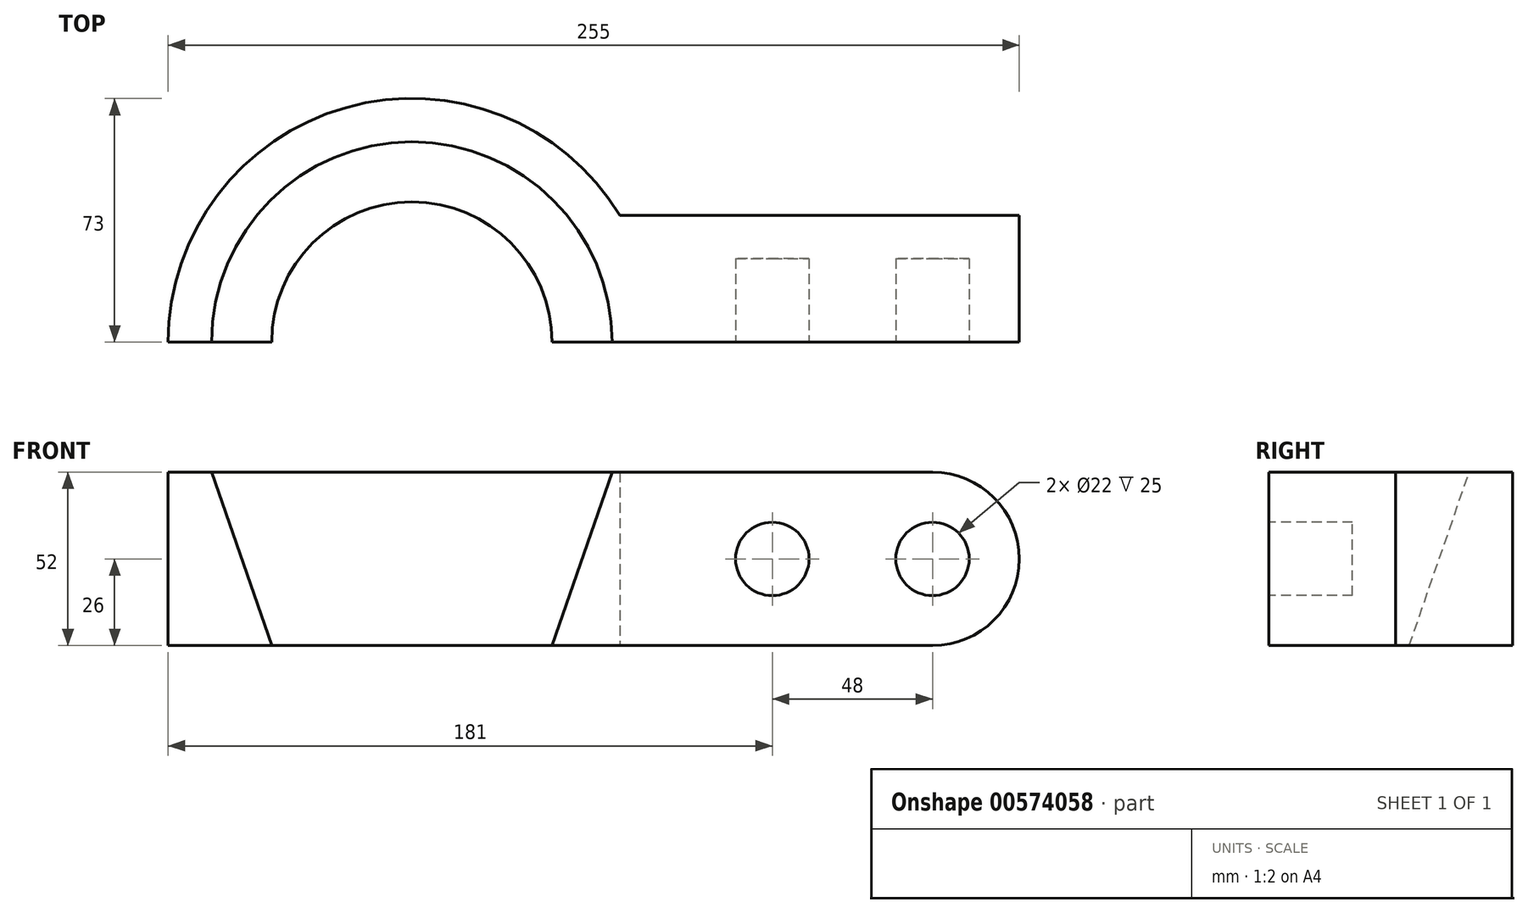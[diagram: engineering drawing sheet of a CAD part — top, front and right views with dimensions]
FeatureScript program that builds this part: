
annotation { "Feature Type Name" : "Feature", "Feature Type Description" : "" }
export const myFeature = defineFeature(function(context is Context, id is Id, definition is map)
    precondition{}
    {
        {
            var Q0;
            Q0=qCreatedBy(makeId("Top.planeOp"),FACE);
            var sketch = newSketch(context, id + "F0", { "sketchPlane" : qUnion([Q0])});
            skArc(sketch, "E0", {"start": v(62.33, 38) * mm, "mid": v(-19.73, 70.28) * mm, "end": v(-73, 0) * mm});
            skLineSegment(sketch, "E1", {"start": v(-73, 0) * mm, "end": v(73, 0) * mm});
            skLineSegment(sketch, "E2", {"start": v(73, 0) * mm, "end": v(182, 0) * mm});
            skLineSegment(sketch, "E3", {"start": v(182, 0) * mm, "end": v(182, 38) * mm});
            skLineSegment(sketch, "E4", {"start": v(182, 38) * mm, "end": v(62.33, 38) * mm});
            skSolve(sketch);
        }
        {
            var Q0;
            Q0=makeQuery(id+"F0.imprint","IMPRINT",FACE,{"disambiguationData":[TD([[makeQuery(id+"F0.imprint","IMPRINT",EDGE,{"derivedFrom":sQuery(id+"F0.wireOp",EDGE,"E0")}),1.0]])]});
            extrude(context, id + "F1", {"entities" : qUnion([Q0]), "depth" : 52 * mm, "offsetDistance" : 25 * mm});
        }
        {
            var Q0;
            Q0=makeQuery(id+"F1.opExtrude","CAP_EDGE",EDGE,{"disambiguationData":[OSD([sQuery(id+"F0.wireOp",EDGE,"E3")])],"isStart":false});
            var Q1;
            Q1=makeQuery(id+"F1.opExtrude","CAP_EDGE",EDGE,{"disambiguationData":[OSD([sQuery(id+"F0.wireOp",EDGE,"E3")])],"isStart":true});
            fillet(context, id + "F2", {"entities" : qUnion([Q0, Q1]), "radius" : 26 * mm, "tangentPropagation" : true, "allowEdgeOverflow" : false});
        }
        {
            var Q0;
            Q0=makeQuery(id+"F1.opExtrude","CAP_FACE",FACE,{"disambiguationData":[OSD([sQuery(id+"F0.wireOp",EDGE,"E0"),sQuery(id+"F0.wireOp",EDGE,"E1"),sQuery(id+"F0.wireOp",EDGE,"E2"),sQuery(id+"F0.wireOp",EDGE,"E3"),sQuery(id+"F0.wireOp",EDGE,"E4")])],"isStart":false});
            var sketch = newSketch(context, id + "F3", { "sketchPlane" : qUnion([Q0])});
            skCircle(sketch, "E5", {"center": v(0, 0) * mm, "radius": 60 * mm});
            skSolve(sketch);
        }
        {
            var Q0;
            Q0=makeQuery(id+"F1.opExtrude","CAP_FACE",FACE,{"disambiguationData":[OSD([sQuery(id+"F0.wireOp",EDGE,"E0"),sQuery(id+"F0.wireOp",EDGE,"E1"),sQuery(id+"F0.wireOp",EDGE,"E2"),sQuery(id+"F0.wireOp",EDGE,"E3"),sQuery(id+"F0.wireOp",EDGE,"E4")])],"isStart":true});
            var sketch = newSketch(context, id + "F4", { "sketchPlane" : qUnion([Q0])});
            skCircle(sketch, "E6", {"center": v(0, 0) * mm, "radius": 42 * mm});
            skSolve(sketch);
        }
        {
            var Q1;
            {var subQ0=sQuery(id+"F3.wireOp",EDGE,"E5");var subQ1=makeQuery(id+"F1.opExtrude","CAP_EDGE",EDGE,{"disambiguationData":[OSD([sQuery(id+"F0.wireOp",EDGE,"E1"),sQuery(id+"F0.wireOp",EDGE,"E2")])],"isStart":false});var subQ2=makeQuery(id+"F3.imprint","INTERSECT",VERTEX,{"disambiguationData":[OD(0.0)],"derivedFrom":[subQ1,subQ0]});Q1=makeQuery(id+"F3.imprint","IMPRINT",FACE,{"disambiguationData":[TD([[makeQuery(id+"F3.imprint","IMPRINT",EDGE,{"disambiguationData":[TD([[subQ2,1.0]])],"derivedFrom":subQ0}),1.0]])]});}
            var Q2;
            {var subQ0=sQuery(id+"F4.wireOp",EDGE,"E6");var subQ1=makeQuery(id+"F1.opExtrude","CAP_EDGE",EDGE,{"disambiguationData":[OSD([sQuery(id+"F0.wireOp",EDGE,"E1"),sQuery(id+"F0.wireOp",EDGE,"E2")])],"isStart":true});var subQ2=makeQuery(id+"F4.imprint","INTERSECT",VERTEX,{"disambiguationData":[OD(0.0)],"derivedFrom":[subQ1,subQ0]});Q2=makeQuery(id+"F4.imprint","IMPRINT",FACE,{"disambiguationData":[TD([[makeQuery(id+"F4.imprint","IMPRINT",EDGE,{"disambiguationData":[TD([[subQ2,-1.0]])],"derivedFrom":subQ0}),1.0]])]});}
            loft(context, id + "F5", {"operationType" : NewBodyOperationType.REMOVE, "sheetProfilesArray" : [{ "sheetProfileEntities" : qUnion([Q1]) }, { "sheetProfileEntities" : qUnion([Q2]) }]});
        }
        {
            var Q0;
            {var subQ1=sQuery(id+"F0.wireOp",EDGE,"E3");var subQ2=sQuery(id+"F0.wireOp",EDGE,"E2");var subQ3=sQuery(id+"F0.wireOp",EDGE,"E1");Q0=makeQuery(id+"F5.boolean.opBoolean","SPLIT",FACE,{"disambiguationData":[TD([makeQuery(id+"F2.opFillet","BLEND_FACE",FACE,{"disambiguationData":[OSD([subQ1])]})])],"derivedFrom":makeQuery(id+"F1.opExtrude","SWEPT_FACE",FACE,{"disambiguationData":[OSD([subQ3,subQ2])]})});}
            var sketch = newSketch(context, id + "F6", { "sketchPlane" : qUnion([Q0])});
            skCircle(sketch, "E7", {"center": v(108, 26) * mm, "radius": 11 * mm});
            skCircle(sketch, "E8", {"center": v(156, 26) * mm, "radius": 11 * mm});
            skSolve(sketch);
        }
        {
            var Q0;
            Q0=makeQuery(id+"F6.imprint","IMPRINT",FACE,{"disambiguationData":[TD([[makeQuery(id+"F6.imprint","IMPRINT",EDGE,{"derivedFrom":sQuery(id+"F6.wireOp",EDGE,"E7")}),1.0]])]});
            var Q1;
            Q1=makeQuery(id+"F6.imprint","IMPRINT",FACE,{"disambiguationData":[TD([[makeQuery(id+"F6.imprint","IMPRINT",EDGE,{"derivedFrom":sQuery(id+"F6.wireOp",EDGE,"E8")}),1.0]])]});
            extrude(context, id + "F7", {"entities" : qUnion([Q0, Q1]), "operationType" : NewBodyOperationType.REMOVE, "oppositeDirection" : true, "depth" : 25 * mm, "offsetDistance" : 25 * mm});
        }
    });
